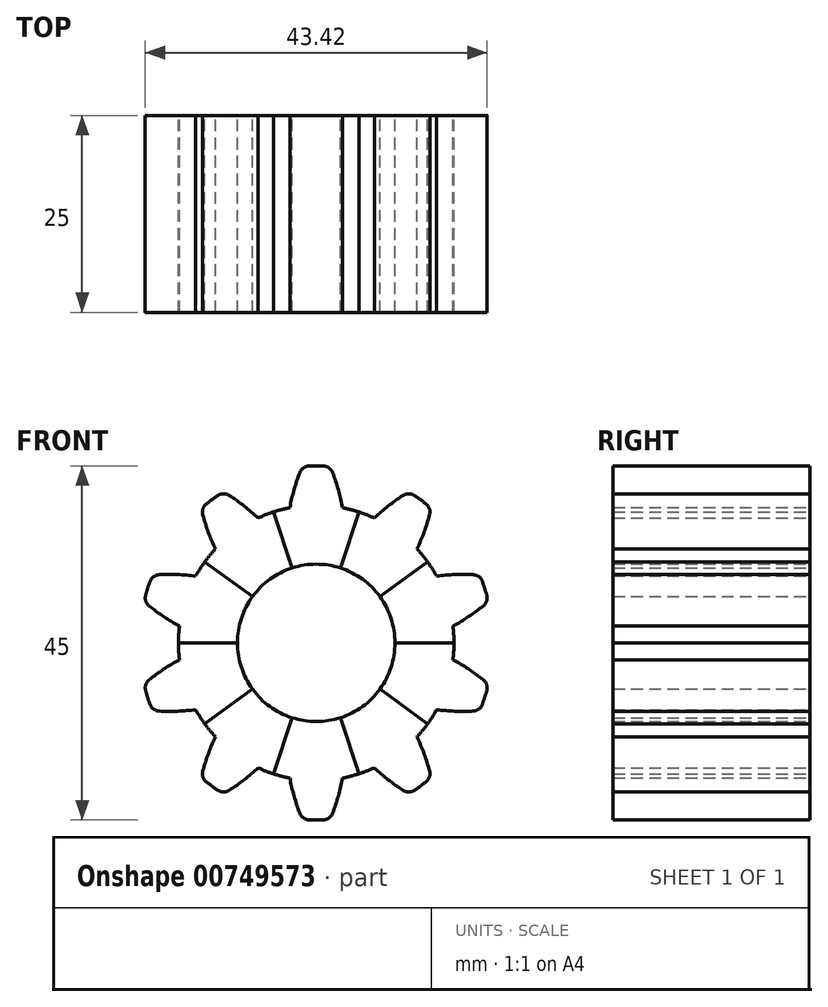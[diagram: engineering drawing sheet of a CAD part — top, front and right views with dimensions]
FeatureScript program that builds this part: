
annotation { "Feature Type Name" : "Feature", "Feature Type Description" : "" }
export const myFeature = defineFeature(function(context is Context, id is Id, definition is map)
    precondition{}
    {
        {
            var Q0;
            Q0=qCreatedBy(makeId("Front.planeOp"),FACE);
            var sketch = newSketch(context, id + "F0", { "sketchPlane" : qUnion([Q0])});
            skCircle(sketch, "E0", {"center": v(0, 0) * mm, "radius": 17.5 * mm, "construction": true});
            skArc(sketch, "E1", {"start": v(3.1, 9.51) * mm, "mid": v(0, 10) * mm, "end": v(-3.1, 9.51) * mm});
            skCircle(sketch, "E2", {"center": v(0, 0) * mm, "radius": 20 * mm, "construction": true});
            skCircle(sketch, "E3", {"center": v(0, 0) * mm, "radius": 22.5 * mm, "construction": true});
            skLineSegment(sketch, "E4", {"start": v(0, 0) * mm, "end": v(0, 22.5) * mm, "construction": true});
            skLineSegment(sketch, "E5", {"start": v(0, 0) * mm, "end": v(1.77, 22.43) * mm, "construction": true});
            skLineSegment(sketch, "E6", {"start": v(0, 0) * mm, "end": v(4.3, 22.09) * mm, "construction": true});
            skLineSegment(sketch, "E7", {"start": v(0, 0) * mm, "end": v(6.95, 21.4) * mm, "construction": true});
            skArc(sketch, "E8", {"start": v(5.4, 16.64) * mm, "mid": v(4.38, 16.94) * mm, "end": v(3.34, 17.18) * mm});
            skArc(sketch, "E9", {"start": v(0.92, 22.48) * mm, "mid": v(0.46, 22.5) * mm, "end": v(0, 22.5) * mm});
            skArc(sketch, "E10", {"start": v(3.34, 17.18) * mm, "mid": v(2.81, 19.44) * mm, "end": v(2.08, 21.65) * mm});
            skArc(sketch, "E11.MirrorCS", {"start": v(-0.92, 22.48) * mm, "mid": v(-0.46, 22.5) * mm, "end": v(0, 22.5) * mm});
            skArc(sketch, "E12.MirrorCS", {"start": v(-3.34, 17.18) * mm, "mid": v(-2.81, 19.44) * mm, "end": v(-2.08, 21.65) * mm});
            skArc(sketch, "E13.MirrorCS", {"start": v(-5.4, 16.64) * mm, "mid": v(-4.38, 16.94) * mm, "end": v(-3.34, 17.18) * mm});
            skLineSegment(sketch, "E14", {"start": v(-3.1, 9.51) * mm, "end": v(-5.4, 16.64) * mm});
            skLineSegment(sketch, "E15", {"start": v(3.1, 9.51) * mm, "end": v(5.4, 16.64) * mm});
            skPoint(sketch, "E16.visualSharp", {"position": v(1.77, 22.43) * mm});
            skArc(sketch, "E16.filletArc", {"start": v(2.08, 21.65) * mm, "mid": v(1.63, 22.24) * mm, "end": v(0.92, 22.48) * mm});
            skPoint(sketch, "E17.visualSharp", {"position": v(-1.77, 22.43) * mm});
            skArc(sketch, "E17.filletArc", {"start": v(-0.92, 22.48) * mm, "mid": v(-1.63, 22.24) * mm, "end": v(-2.08, 21.65) * mm});
            skSolve(sketch);
        }
        {
            var Q0;
            Q0=qSketchRegion(id+"F0",true);
            extrude(context, id + "F1", {"entities" : qUnion([Q0]), "depth" : 25 * mm, "offsetDistance" : 25 * mm});
        }
        {
            var Q0;
            Q0=makeQuery(id+"F1.opExtrude","SWEPT_BODY",BODY,{"disambiguationData":[OSD([sQuery(id+"F0.wireOp",EDGE,"E1"),sQuery(id+"F0.wireOp",EDGE,"E8"),sQuery(id+"F0.wireOp",EDGE,"E9"),sQuery(id+"F0.wireOp",EDGE,"E10"),sQuery(id+"F0.wireOp",EDGE,"E11.MirrorCS"),sQuery(id+"F0.wireOp",EDGE,"E12.MirrorCS"),sQuery(id+"F0.wireOp",EDGE,"E13.MirrorCS"),sQuery(id+"F0.wireOp",EDGE,"E14"),sQuery(id+"F0.wireOp",EDGE,"E15")])]});
            var Q1;
            Q1=makeQuery(id+"F1.opExtrude","SWEPT_FACE",FACE,{"disambiguationData":[OSD([sQuery(id+"F0.wireOp",EDGE,"E1")])]});
            circularPattern(context, id + "F2", {"entities" : qUnion([Q0]), "axis" : qUnion([Q1]), "angle" : 360 * degree, "instanceCount" : 10, "equalSpace" : true, "isCentered" : true});
        }
    });
